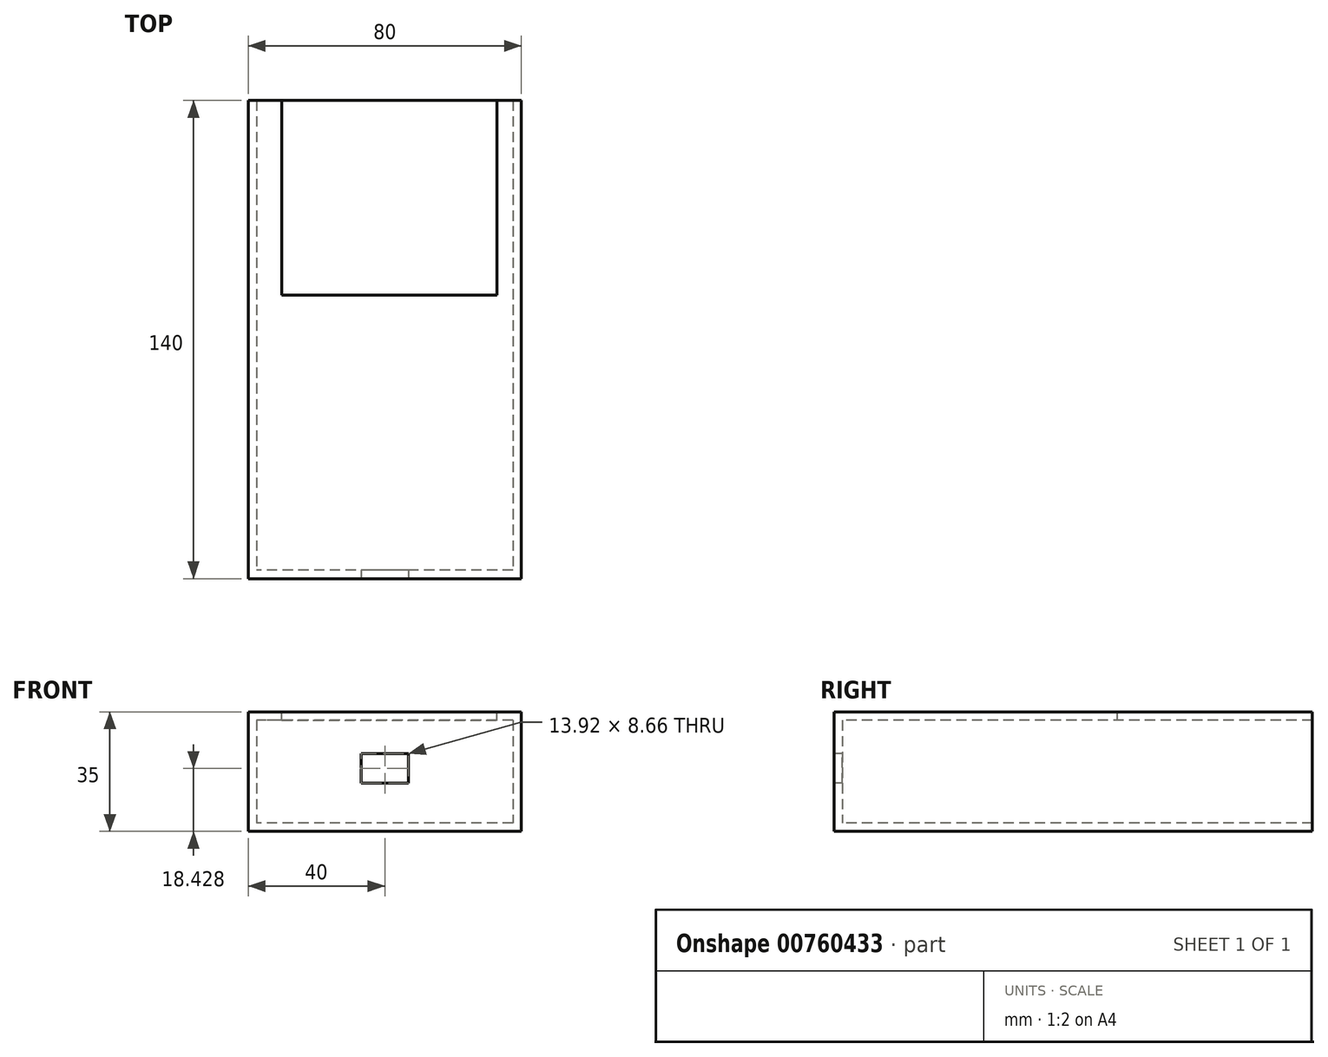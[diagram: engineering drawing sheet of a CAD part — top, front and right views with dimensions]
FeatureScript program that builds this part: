
annotation { "Feature Type Name" : "Feature", "Feature Type Description" : "" }
export const myFeature = defineFeature(function(context is Context, id is Id, definition is map)
    precondition{}
    {
        {
            var Q0;
            Q0=qCreatedBy(makeId("Top.planeOp"),FACE);
            var sketch = newSketch(context, id + "F0", { "sketchPlane" : qUnion([Q0])});
            skLineSegment(sketch, "E0.bottom", {"start": v(40, 70) * mm, "end": v(-40, 70) * mm});
            skLineSegment(sketch, "E0.top", {"start": v(40, -70) * mm, "end": v(-40, -70) * mm});
            skLineSegment(sketch, "E0.left", {"start": v(40, 70) * mm, "end": v(40, -70) * mm});
            skLineSegment(sketch, "E0.right", {"start": v(-40, 70) * mm, "end": v(-40, -70) * mm});
            skPoint(sketch, "E0.middle", {"position": v(0, 0) * mm});
            skSolve(sketch);
        }
        {
            var Q0;
            Q0 = qSketchRegion(id + "F0", true);
            extrude(context, id + "F1", {"entities" : qUnion([Q0]), "depth" : 35 * mm, "offsetDistance" : 25 * mm});
        }
        {
            var Q0;
            Q0=makeQuery(id+"F1.opExtrude","SWEPT_FACE",FACE,{"disambiguationData":[OSD([sQuery(id+"F0.wireOp",EDGE,"E0.bottom")])]});
            shell(context, id + "F2", {"entities" : qUnion([Q0]), "thickness" : 2.5 * mm});
        }
        {
            var Q0;
            Q0=makeQuery(id+"F1.opExtrude","CAP_FACE",FACE,{"disambiguationData":[OSD([sQuery(id+"F0.wireOp",EDGE,"E0.bottom"),sQuery(id+"F0.wireOp",EDGE,"E0.top"),sQuery(id+"F0.wireOp",EDGE,"E0.left"),sQuery(id+"F0.wireOp",EDGE,"E0.right")])],"isStart":false});
            var sketch = newSketch(context, id + "F3", { "sketchPlane" : qUnion([Q0])});
            skLineSegment(sketch, "E1.bottom", {"start": v(-30.17, 70) * mm, "end": v(32.83, 70) * mm});
            skLineSegment(sketch, "E1.top", {"start": v(-30.17, 13) * mm, "end": v(32.83, 13) * mm});
            skLineSegment(sketch, "E1.left", {"start": v(-30.17, 70) * mm, "end": v(-30.17, 13) * mm});
            skLineSegment(sketch, "E1.right", {"start": v(32.83, 70) * mm, "end": v(32.83, 13) * mm});
            skSolve(sketch);
        }
        {
            var Q0;
            Q0 = qSketchRegion(id + "F3", true);
            extrude(context, id + "F4", {"entities" : qUnion([Q0]), "operationType" : NewBodyOperationType.REMOVE, "oppositeDirection" : true, "depth" : 2.5 * mm, "offsetDistance" : 25 * mm});
        }
        {
            var Q0;
            Q0=makeQuery(id+"F1.opExtrude","SWEPT_FACE",FACE,{"disambiguationData":[OSD([sQuery(id+"F0.wireOp",EDGE,"E0.top")])]});
            var sketch = newSketch(context, id + "F5", { "sketchPlane" : qUnion([Q0])});
            skLineSegment(sketch, "E2.bottom", {"start": v(6.96, 14.1) * mm, "end": v(-6.96, 14.1) * mm});
            skLineSegment(sketch, "E2.top", {"start": v(6.96, 22.76) * mm, "end": v(-6.96, 22.76) * mm});
            skLineSegment(sketch, "E2.left", {"start": v(6.96, 14.1) * mm, "end": v(6.96, 22.76) * mm});
            skLineSegment(sketch, "E2.right", {"start": v(-6.96, 14.1) * mm, "end": v(-6.96, 22.76) * mm});
            skPoint(sketch, "E2.middle", {"position": v(0, 18.43) * mm});
            skSolve(sketch);
        }
        {
            var Q0;
            Q0 = qSketchRegion(id + "F5", true);
            extrude(context, id + "F6", {"entities" : qUnion([Q0]), "operationType" : NewBodyOperationType.REMOVE, "endBound" : BoundingType.THROUGH_ALL, "oppositeDirection" : true, "depth" : 25 * mm, "offsetDistance" : 25 * mm});
        }
    });
